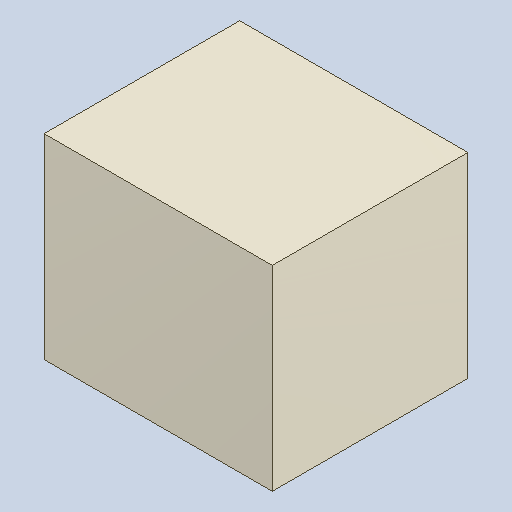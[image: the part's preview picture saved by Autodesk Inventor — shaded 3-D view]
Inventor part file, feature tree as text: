
AUTODESK INVENTOR PART (.ipt)
format: ipt  version: 2023.4 (Build 274418000, 418)  size: 82,432 bytes
history: native  units: mm
features: extrude x1
ambient origin geometry x8: Origin, YZ Plane, XZ Plane, XY Plane, X Axis, Y Axis, Z Axis, Center Point
bodies: Solid1 (feature_tree)
feature tree (1):
  extrude  "Extruded_12"  [1 undecoded]
note: 1 required parameter value undecoded (feature->parameter linkage not recoverable at this tier; creation-order binding heuristic only, values carry confidence <= 0.55)
